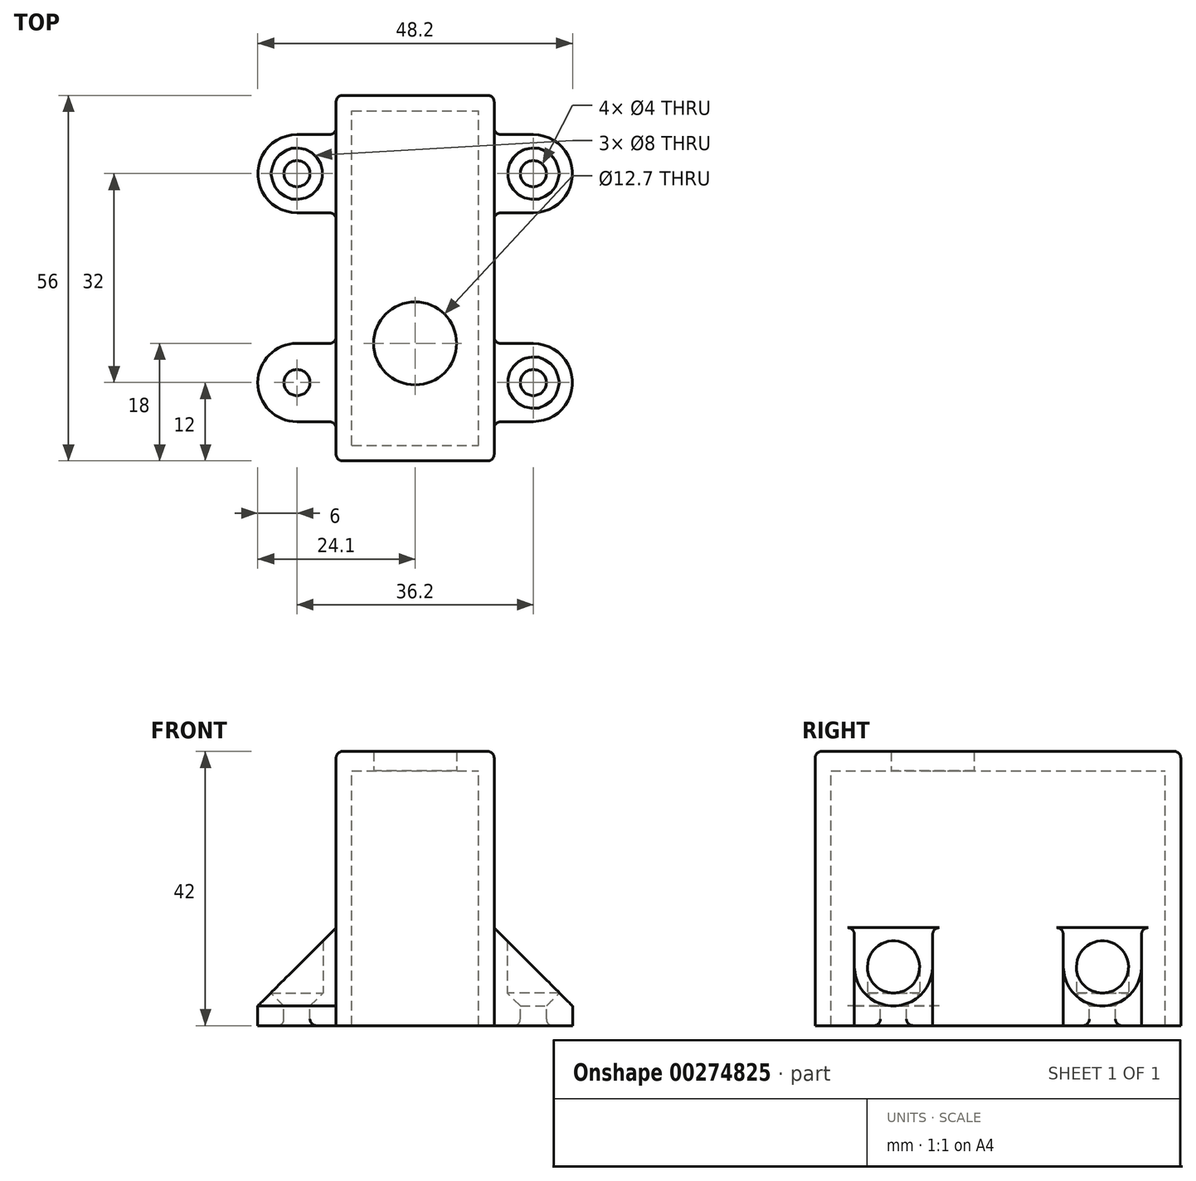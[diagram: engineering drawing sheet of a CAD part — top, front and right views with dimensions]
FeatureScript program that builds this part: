
annotation { "Feature Type Name" : "Feature", "Feature Type Description" : "" }
export const myFeature = defineFeature(function(context is Context, id is Id, definition is map)
    precondition{}
    {
        {
            var Q0;
            Q0=qCreatedBy(makeId("Top.planeOp"),FACE);
            var sketch = newSketch(context, id + "F0", { "sketchPlane" : qUnion([Q0])});
            skCircle(sketch, "E0", {"center": v(0, 0) * mm, "radius": 6.35 * mm});
            skLineSegment(sketch, "E1.bottom", {"start": v(8.1, 14) * mm, "end": v(-8.1, 14) * mm, "construction": true});
            skLineSegment(sketch, "E1.top", {"start": v(8.1, -14) * mm, "end": v(-8.1, -14) * mm, "construction": true});
            skLineSegment(sketch, "E1.left", {"start": v(8.1, 14) * mm, "end": v(8.1, -14) * mm, "construction": true});
            skLineSegment(sketch, "E1.right", {"start": v(-8.1, 14) * mm, "end": v(-8.1, -14) * mm, "construction": true});
            skCircle(sketch, "E2", {"center": v(0, 0) * mm, "radius": 5.9 * mm, "construction": true});
            skLineSegment(sketch, "E3.bottom", {"start": v(-7.1, 14) * mm, "end": v(-0.8, 14) * mm, "construction": true});
            skLineSegment(sketch, "E3.top", {"start": v(-7.1, 22.65) * mm, "end": v(-0.8, 22.65) * mm, "construction": true});
            skLineSegment(sketch, "E3.left", {"start": v(-7.1, 14) * mm, "end": v(-7.1, 22.65) * mm, "construction": true});
            skLineSegment(sketch, "E3.right", {"start": v(-0.8, 14) * mm, "end": v(-0.8, 22.65) * mm, "construction": true});
            skSolve(sketch);
        }
        {
            var Q0;
            Q0=qCreatedBy(makeId("Top.planeOp"),FACE);
            var sketch = newSketch(context, id + "F1", { "sketchPlane" : qUnion([Q0])});
            skLineSegment(sketch, "E4.bottom", {"start": v(12.1, 38) * mm, "end": v(-12.1, 38) * mm});
            skLineSegment(sketch, "E4.top", {"start": v(12.1, -18) * mm, "end": v(-12.1, -18) * mm});
            skLineSegment(sketch, "E4.left", {"start": v(12.1, 38) * mm, "end": v(12.1, -18) * mm});
            skLineSegment(sketch, "E4.right", {"start": v(-12.1, 38) * mm, "end": v(-12.1, -18) * mm});
            skPoint(sketch, "E4.middle", {"position": v(0, 10) * mm});
            skSolve(sketch);
        }
        {
            var Q0;
            Q0 = qSketchRegion(id + "F1", true);
            extrude(context, id + "F2", {"entities" : qUnion([Q0]), "depth" : 3 * mm});
        }
        {
            var Q0;
            Q0 = qSketchRegion(id + "F0", true);
            var Q1;
            Q1=makeQuery(id+"F2.opExtrude","CAP_FACE",FACE,{"disambiguationData":[OSD([sQuery(id+"F1.wireOp",EDGE,"E4.bottom"),sQuery(id+"F1.wireOp",EDGE,"E4.top"),sQuery(id+"F1.wireOp",EDGE,"E4.left"),sQuery(id+"F1.wireOp",EDGE,"E4.right")])],"isStart":false});
            extrude(context, id + "F3", {"entities" : qUnion([Q0]), "operationType" : NewBodyOperationType.REMOVE, "endBound" : BoundingType.UP_TO_SURFACE, "endBoundEntityFace" : qUnion([Q1]), "depth" : 25 * mm});
        }
        {
            var Q0;
            Q0=makeQuery(id+"F2.opExtrude","CAP_FACE",FACE,{"disambiguationData":[OSD([sQuery(id+"F1.wireOp",EDGE,"E4.bottom"),sQuery(id+"F1.wireOp",EDGE,"E4.top"),sQuery(id+"F1.wireOp",EDGE,"E4.left"),sQuery(id+"F1.wireOp",EDGE,"E4.right")])],"isStart":true});
            var sketch = newSketch(context, id + "F4", { "sketchPlane" : qUnion([Q0])});
            skLineSegment(sketch, "E5.bottom", {"start": v(-12.1, 18) * mm, "end": v(12.1, 18) * mm});
            skLineSegment(sketch, "E5.top", {"start": v(-12.1, -38) * mm, "end": v(12.1, -38) * mm});
            skLineSegment(sketch, "E5.left", {"start": v(-12.1, 18) * mm, "end": v(-12.1, -38) * mm});
            skLineSegment(sketch, "E5.right", {"start": v(12.1, 18) * mm, "end": v(12.1, -38) * mm});
            skLineSegment(sketch, "E6.bottom", {"start": v(-9.7, 15.6) * mm, "end": v(9.7, 15.6) * mm});
            skLineSegment(sketch, "E6.top", {"start": v(-9.7, -35.6) * mm, "end": v(9.7, -35.6) * mm});
            skLineSegment(sketch, "E6.left", {"start": v(-9.7, 15.6) * mm, "end": v(-9.7, -35.6) * mm});
            skLineSegment(sketch, "E6.right", {"start": v(9.7, 15.6) * mm, "end": v(9.7, -35.6) * mm});
            skSolve(sketch);
        }
        {
            var Q0;
            Q0 = qSketchRegion(id + "F4", true);
            extrude(context, id + "F5", {"entities" : qUnion([Q0]), "operationType" : NewBodyOperationType.ADD, "depth" : 36 * mm});
        }
        {
            var Q0;
            Q0=makeQuery(id+"F5.opExtrude","CAP_FACE",FACE,{"disambiguationData":[OSD([sQuery(id+"F4.wireOp",EDGE,"E5.bottom"),sQuery(id+"F4.wireOp",EDGE,"E5.top"),sQuery(id+"F4.wireOp",EDGE,"E5.left"),sQuery(id+"F4.wireOp",EDGE,"E5.right"),sQuery(id+"F4.wireOp",EDGE,"E6.bottom"),sQuery(id+"F4.wireOp",EDGE,"E6.top"),sQuery(id+"F4.wireOp",EDGE,"E6.left"),sQuery(id+"F4.wireOp",EDGE,"E6.right")])],"isStart":false});
            var sketch = newSketch(context, id + "F6", { "sketchPlane" : qUnion([Q0])});
            skLineSegment(sketch, "E7.bottom", {"start": v(-9.7, 15.6) * mm, "end": v(9.7, 15.6) * mm});
            skLineSegment(sketch, "E7.top", {"start": v(-9.7, -35.6) * mm, "end": v(9.7, -35.6) * mm});
            skLineSegment(sketch, "E7.left", {"start": v(-9.7, 15.6) * mm, "end": v(-9.7, -35.6) * mm});
            skLineSegment(sketch, "E7.right", {"start": v(9.7, 15.6) * mm, "end": v(9.7, -35.6) * mm});
            skLineSegment(sketch, "E8.bottom", {"start": v(-12.1, 18) * mm, "end": v(12.1, 18) * mm});
            skLineSegment(sketch, "E8.top", {"start": v(-12.1, -38) * mm, "end": v(12.1, -38) * mm});
            skLineSegment(sketch, "E8.left", {"start": v(-12.1, 18) * mm, "end": v(-12.1, 12) * mm});
            skLineSegment(sketch, "E8.right", {"start": v(12.1, 18) * mm, "end": v(12.1, -38) * mm});
            skArc(sketch, "E9", {"start": v(-18.1, 12) * mm, "mid": v(-24.1, 6) * mm, "end": v(-18.1, 0) * mm});
            skPoint(sketch, "E9.centerSnap0", {"position": v(-12.1, 6) * mm});
            skLineSegment(sketch, "E10.bottom", {"start": v(-18.1, 12) * mm, "end": v(-12.1, 12) * mm});
            skLineSegment(sketch, "E10.top", {"start": v(-18.1, 0) * mm, "end": v(-12.1, 0) * mm});
            skCircle(sketch, "E11", {"center": v(-18.1, 6) * mm, "radius": 2 * mm});
            skPoint(sketch, "E12.orphan", {"position": v(-6.1, 12) * mm});
            skPoint(sketch, "E13.orphan", {"position": v(-6.1, 0) * mm});
            skLineSegment(sketch, "E14.trimOffspring", {"start": v(-12.1, 0) * mm, "end": v(-12.1, -38) * mm});
            skLineSegment(sketch, "E15.MirrorCS", {"start": v(18.1, 12) * mm, "end": v(12.1, 12) * mm});
            skArc(sketch, "E16.MirrorCS", {"start": v(18.1, 12) * mm, "mid": v(24.1, 6) * mm, "end": v(18.1, 0) * mm});
            skLineSegment(sketch, "E17.MirrorCS", {"start": v(18.1, 0) * mm, "end": v(12.1, 0) * mm});
            skCircle(sketch, "E18.MirrorC", {"center": v(18.1, 6) * mm, "radius": 2 * mm});
            skLineSegment(sketch, "E19", {"start": v(38.2, 6) * mm, "end": v(-42.21, 6) * mm, "construction": true});
            skLineSegment(sketch, "E20", {"start": v(37.28, -10) * mm, "end": v(-33.25, -10) * mm, "construction": true});
            skPoint(sketch, "E20.startSnap0", {"position": v(12.1, -10) * mm});
            skLineSegment(sketch, "E21.MirrorCS", {"start": v(18.1, -20) * mm, "end": v(12.1, -20) * mm});
            skArc(sketch, "E22.MirrorCS", {"start": v(18.1, -32) * mm, "mid": v(24.1, -26) * mm, "end": v(18.1, -20) * mm});
            skLineSegment(sketch, "E23.MirrorCS", {"start": v(18.1, -32) * mm, "end": v(12.1, -32) * mm});
            skCircle(sketch, "E24.MirrorC", {"center": v(18.1, -26) * mm, "radius": 2 * mm});
            skLineSegment(sketch, "E25.MirrorCS", {"start": v(38.2, -26) * mm, "end": v(-42.21, -26) * mm, "construction": true});
            skLineSegment(sketch, "E26.MirrorCS", {"start": v(-18.1, -32) * mm, "end": v(-12.1, -32) * mm});
            skArc(sketch, "E27.MirrorCS", {"start": v(-18.1, -32) * mm, "mid": v(-24.1, -26) * mm, "end": v(-18.1, -20) * mm});
            skLineSegment(sketch, "E28.MirrorCS", {"start": v(-18.1, -20) * mm, "end": v(-12.1, -20) * mm});
            skCircle(sketch, "E29.MirrorC", {"center": v(-18.1, -26) * mm, "radius": 2 * mm});
            skSolve(sketch);
        }
        {
            var Q0;
            Q0 = qSketchRegion(id + "F6", true);
            extrude(context, id + "F7", {"entities" : qUnion([Q0]), "operationType" : NewBodyOperationType.ADD, "depth" : 3 * mm});
        }
        {
            var Q0;
            {var subQ2=sQuery(id+"F6.wireOp",EDGE,"E26.MirrorCS");var subQ6=sQuery(id+"F4.wireOp",EDGE,"E5.left");var subQ7=makeQuery(id+"F5.opExtrude","CAP_EDGE",EDGE,{"disambiguationData":[OSD([subQ6])],"isStart":false});Q0=makeQuery(id+"F7.boolean.opBoolean","SPLIT",EDGE,{"disambiguationData":[TD([makeQuery(id+"F7.opExtrude","SWEPT_FACE",FACE,{"disambiguationData":[OSD([subQ2])]})])],"derivedFrom":subQ7});}
            var Q1;
            {var subQ5=sQuery(id+"F6.wireOp",EDGE,"E10.bottom");var subQ7=sQuery(id+"F4.wireOp",EDGE,"E5.left");var subQ8=makeQuery(id+"F5.opExtrude","CAP_EDGE",EDGE,{"disambiguationData":[OSD([subQ7])],"isStart":false});Q1=makeQuery(id+"F7.boolean.opBoolean","SPLIT",EDGE,{"disambiguationData":[TD([makeQuery(id+"F7.opExtrude","SWEPT_FACE",FACE,{"disambiguationData":[OSD([subQ5])]})])],"derivedFrom":subQ8});}
            var Q2;
            {var subQ5=sQuery(id+"F6.wireOp",EDGE,"E15.MirrorCS");var subQ7=sQuery(id+"F4.wireOp",EDGE,"E5.right");Q2=makeQuery(id+"F7.boolean.opBoolean","SPLIT",EDGE,{"disambiguationData":[TD([makeQuery(id+"F7.opExtrude","SWEPT_FACE",FACE,{"disambiguationData":[OSD([subQ5])]})])],"derivedFrom":makeQuery(id+"F5.opExtrude","CAP_EDGE",EDGE,{"disambiguationData":[OSD([subQ7])],"isStart":false})});}
            var Q3;
            {var subQ3=sQuery(id+"F6.wireOp",EDGE,"E21.MirrorCS");var subQ7=sQuery(id+"F4.wireOp",EDGE,"E5.right");Q3=makeQuery(id+"F7.boolean.opBoolean","SPLIT",EDGE,{"disambiguationData":[TD([makeQuery(id+"F7.opExtrude","SWEPT_FACE",FACE,{"disambiguationData":[OSD([subQ3])]})])],"derivedFrom":makeQuery(id+"F5.opExtrude","CAP_EDGE",EDGE,{"disambiguationData":[OSD([subQ7])],"isStart":false})});}
            chamfer(context, id + "F8", {"entities" : qUnion([Q0, Q1, Q2, Q3]), "width" : 12 * mm, "tangentPropagation" : true});
        }
        {
            var Q0;
            Q0=makeQuery(id+"F7.opExtrude","CAP_FACE",FACE,{"disambiguationData":[OSD([sQuery(id+"F6.wireOp",EDGE,"E7.bottom"),sQuery(id+"F6.wireOp",EDGE,"E7.top"),sQuery(id+"F6.wireOp",EDGE,"E7.left"),sQuery(id+"F6.wireOp",EDGE,"E7.right"),sQuery(id+"F6.wireOp",EDGE,"E8.bottom"),sQuery(id+"F6.wireOp",EDGE,"E8.top"),sQuery(id+"F6.wireOp",EDGE,"E8.left"),sQuery(id+"F6.wireOp",EDGE,"E8.right"),sQuery(id+"F6.wireOp",EDGE,"E9"),sQuery(id+"F6.wireOp",EDGE,"E10.bottom"),sQuery(id+"F6.wireOp",EDGE,"E10.top"),sQuery(id+"F6.wireOp",EDGE,"E11"),sQuery(id+"F6.wireOp",EDGE,"E14.trimOffspring"),sQuery(id+"F6.wireOp",EDGE,"E15.MirrorCS"),sQuery(id+"F6.wireOp",EDGE,"E16.MirrorCS"),sQuery(id+"F6.wireOp",EDGE,"E17.MirrorCS"),sQuery(id+"F6.wireOp",EDGE,"E18.MirrorC"),sQuery(id+"F6.wireOp",EDGE,"E21.MirrorCS"),sQuery(id+"F6.wireOp",EDGE,"E22.MirrorCS"),sQuery(id+"F6.wireOp",EDGE,"E23.MirrorCS"),sQuery(id+"F6.wireOp",EDGE,"E24.MirrorC"),sQuery(id+"F6.wireOp",EDGE,"E26.MirrorCS"),sQuery(id+"F6.wireOp",EDGE,"E27.MirrorCS"),sQuery(id+"F6.wireOp",EDGE,"E28.MirrorCS"),sQuery(id+"F6.wireOp",EDGE,"E29.MirrorC")])],"isStart":false});
            cPlane(context, id + "F9", {"entities" : qUnion([Q0]), "cplaneType" : CPlaneType.OFFSET, "offset" : 3 * mm, "oppositeDirection" : true, "width" : 150 * mm, "height" : 150 * mm});
        }
        {
            var Q0;
            Q0=qCreatedBy(id+"F9.planeOp",FACE);
            var sketch = newSketch(context, id + "F10", { "sketchPlane" : qUnion([Q0])});
            skLineSegment(sketch, "E30", {"start": v(18.1, -42.57) * mm, "end": v(18.1, 21.83) * mm, "construction": true});
            skLineSegment(sketch, "E31", {"start": v(-18.1, -40.05) * mm, "end": v(-18.1, 19.87) * mm, "construction": true});
            skLineSegment(sketch, "E32", {"start": v(28.5, -26) * mm, "end": v(-28.53, -26) * mm, "construction": true});
            skLineSegment(sketch, "E33", {"start": v(28.5, 6) * mm, "end": v(-28.53, 6) * mm, "construction": true});
            skCircle(sketch, "E34", {"center": v(18.1, -26) * mm, "radius": 4 * mm});
            skCircle(sketch, "E35", {"center": v(18.1, 6) * mm, "radius": 4 * mm});
            skCircle(sketch, "E36", {"center": v(-18.1, -26) * mm, "radius": 4 * mm});
            skCircle(sketch, "E37", {"center": v(-18.1, 6) * mm, "radius": 4 * mm});
            skSolve(sketch);
        }
        {
            var Q0;
            Q0 = qSketchRegion(id + "F10", true);
            var Q1;
            {var subQ2=sQuery(id+"F6.wireOp",EDGE,"E26.MirrorCS");var subQ6=sQuery(id+"F4.wireOp",EDGE,"E5.left");var subQ7=makeQuery(id+"F5.opExtrude","CAP_EDGE",EDGE,{"disambiguationData":[OSD([subQ6])],"isStart":false});Q1=makeQuery(id+"F8.opChamfer","BLEND_FACE",FACE,{"disambiguationData":[OSD([subQ6]),TDD([makeQuery(id+"F7.boolean.opBoolean","SPLIT",EDGE,{"disambiguationData":[TD([makeQuery(id+"F7.opExtrude","SWEPT_FACE",FACE,{"disambiguationData":[OSD([subQ2])]})])],"derivedFrom":subQ7})])]});}
            extrude(context, id + "F11", {"entities" : qUnion([Q0]), "operationType" : NewBodyOperationType.REMOVE, "endBound" : BoundingType.UP_TO_SURFACE, "oppositeDirection" : true, "endBoundEntityFace" : qUnion([Q1]), "depth" : 25 * mm});
        }
        {
            var Q0;
            Q0=makeQuery(id+"F11.boolean.opBoolean","COPY",EDGE,{"derivedFrom":makeQuery(id+"F11.opExtrude","CAP_EDGE",EDGE,{"disambiguationData":[OSD([sQuery(id+"F10.wireOp",EDGE,"E35")])],"isStart":true})});
            var Q1;
            Q1=makeQuery(id+"F11.boolean.opBoolean","COPY",EDGE,{"derivedFrom":makeQuery(id+"F11.opExtrude","CAP_EDGE",EDGE,{"disambiguationData":[OSD([sQuery(id+"F10.wireOp",EDGE,"E34")])],"isStart":true})});
            var Q2;
            Q2=makeQuery(id+"F11.boolean.opBoolean","COPY",EDGE,{"derivedFrom":makeQuery(id+"F11.opExtrude","CAP_EDGE",EDGE,{"disambiguationData":[OSD([sQuery(id+"F10.wireOp",EDGE,"E37")])],"isStart":true})});
            var Q3;
            Q3=makeQuery(id+"F11.boolean.opBoolean","COPY",EDGE,{"derivedFrom":makeQuery(id+"F11.opExtrude","CAP_EDGE",EDGE,{"disambiguationData":[OSD([sQuery(id+"F10.wireOp",EDGE,"E36")])],"isStart":true})});
            chamfer(context, id + "F12", {"entities" : qUnion([Q0, Q1, Q2, Q3]), "width" : 2 * mm, "tangentPropagation" : true});
        }
        {
            var Q0;
            Q0=makeQuery(id+"F7.boolean.opBoolean","MERGE",EDGE,{"derivedFrom":[makeQuery(id+"F5.boolean.opBoolean","MERGE",EDGE,{"derivedFrom":[makeQuery(id+"F2.opExtrude","SWEPT_EDGE",EDGE,{"disambiguationData":[OSD([sQuery(id+"F1.wireOp",EDGE,"E4.bottom"),sQuery(id+"F1.wireOp",EDGE,"E4.right")])]}),makeQuery(id+"F5.opExtrude","SWEPT_EDGE",EDGE,{"disambiguationData":[OSD([sQuery(id+"F4.wireOp",EDGE,"E5.top"),sQuery(id+"F4.wireOp",EDGE,"E5.left")])]})]}),makeQuery(id+"F7.opExtrude","SWEPT_EDGE",EDGE,{"disambiguationData":[OSD([sQuery(id+"F6.wireOp",EDGE,"E8.top"),sQuery(id+"F6.wireOp",EDGE,"E14.trimOffspring")])]})]});
            var Q1;
            Q1=makeQuery(id+"F7.boolean.opBoolean","MERGE",EDGE,{"derivedFrom":[makeQuery(id+"F5.boolean.opBoolean","MERGE",EDGE,{"derivedFrom":[makeQuery(id+"F2.opExtrude","SWEPT_EDGE",EDGE,{"disambiguationData":[OSD([sQuery(id+"F1.wireOp",EDGE,"E4.bottom"),sQuery(id+"F1.wireOp",EDGE,"E4.left")])]}),makeQuery(id+"F5.opExtrude","SWEPT_EDGE",EDGE,{"disambiguationData":[OSD([sQuery(id+"F4.wireOp",EDGE,"E5.top"),sQuery(id+"F4.wireOp",EDGE,"E5.right")])]})]}),makeQuery(id+"F7.opExtrude","SWEPT_EDGE",EDGE,{"disambiguationData":[OSD([sQuery(id+"F6.wireOp",EDGE,"E8.top"),sQuery(id+"F6.wireOp",EDGE,"E8.right")])]})]});
            var Q2;
            Q2=makeQuery(id+"F2.opExtrude","CAP_EDGE",EDGE,{"disambiguationData":[OSD([sQuery(id+"F1.wireOp",EDGE,"E4.bottom")])],"isStart":false});
            var Q3;
            Q3=makeQuery(id+"F2.opExtrude","CAP_EDGE",EDGE,{"disambiguationData":[OSD([sQuery(id+"F1.wireOp",EDGE,"E4.right")])],"isStart":false});
            var Q4;
            Q4=makeQuery(id+"F2.opExtrude","CAP_EDGE",EDGE,{"disambiguationData":[OSD([sQuery(id+"F1.wireOp",EDGE,"E4.left")])],"isStart":false});
            var Q5;
            Q5=makeQuery(id+"F2.opExtrude","CAP_EDGE",EDGE,{"disambiguationData":[OSD([sQuery(id+"F1.wireOp",EDGE,"E4.top")])],"isStart":false});
            var Q6;
            Q6=makeQuery(id+"F7.boolean.opBoolean","MERGE",EDGE,{"derivedFrom":[makeQuery(id+"F5.boolean.opBoolean","MERGE",EDGE,{"derivedFrom":[makeQuery(id+"F2.opExtrude","SWEPT_EDGE",EDGE,{"disambiguationData":[OSD([sQuery(id+"F1.wireOp",EDGE,"E4.top"),sQuery(id+"F1.wireOp",EDGE,"E4.left")])]}),makeQuery(id+"F5.opExtrude","SWEPT_EDGE",EDGE,{"disambiguationData":[OSD([sQuery(id+"F4.wireOp",EDGE,"E5.bottom"),sQuery(id+"F4.wireOp",EDGE,"E5.right")])]})]}),makeQuery(id+"F7.opExtrude","SWEPT_EDGE",EDGE,{"disambiguationData":[OSD([sQuery(id+"F6.wireOp",EDGE,"E8.bottom"),sQuery(id+"F6.wireOp",EDGE,"E8.right")])]})]});
            var Q7;
            Q7=makeQuery(id+"F7.boolean.opBoolean","MERGE",EDGE,{"derivedFrom":[makeQuery(id+"F5.boolean.opBoolean","MERGE",EDGE,{"derivedFrom":[makeQuery(id+"F2.opExtrude","SWEPT_EDGE",EDGE,{"disambiguationData":[OSD([sQuery(id+"F1.wireOp",EDGE,"E4.top"),sQuery(id+"F1.wireOp",EDGE,"E4.right")])]}),makeQuery(id+"F5.opExtrude","SWEPT_EDGE",EDGE,{"disambiguationData":[OSD([sQuery(id+"F4.wireOp",EDGE,"E5.bottom"),sQuery(id+"F4.wireOp",EDGE,"E5.left")])]})]}),makeQuery(id+"F7.opExtrude","SWEPT_EDGE",EDGE,{"disambiguationData":[OSD([sQuery(id+"F6.wireOp",EDGE,"E8.bottom"),sQuery(id+"F6.wireOp",EDGE,"E8.left")])]})]});
            var Q8;
            Q8=makeQuery(id+"F7.opExtrude","SWEPT_EDGE",EDGE,{"disambiguationData":[OSD([sQuery(id+"F6.wireOp",EDGE,"E14.trimOffspring"),sQuery(id+"F6.wireOp",EDGE,"E26.MirrorCS")])]});
            var Q9;
            Q9=makeQuery(id+"F7.opExtrude","SWEPT_EDGE",EDGE,{"disambiguationData":[OSD([sQuery(id+"F4.wireOp",EDGE,"E5.left"),sQuery(id+"F6.wireOp",EDGE,"E10.top"),sQuery(id+"F6.wireOp",EDGE,"E14.trimOffspring")])]});
            var Q10;
            Q10=makeQuery(id+"F7.opExtrude","SWEPT_EDGE",EDGE,{"disambiguationData":[OSD([sQuery(id+"F6.wireOp",EDGE,"E14.trimOffspring"),sQuery(id+"F6.wireOp",EDGE,"E28.MirrorCS")])]});
            var Q11;
            Q11=makeQuery(id+"F7.opExtrude","SWEPT_EDGE",EDGE,{"disambiguationData":[OSD([sQuery(id+"F4.wireOp",EDGE,"E5.left"),sQuery(id+"F6.wireOp",EDGE,"E8.left"),sQuery(id+"F6.wireOp",EDGE,"E10.bottom")])]});
            var Q12;
            Q12=makeQuery(id+"F7.opExtrude","SWEPT_EDGE",EDGE,{"disambiguationData":[OSD([sQuery(id+"F6.wireOp",EDGE,"E8.right"),sQuery(id+"F6.wireOp",EDGE,"E15.MirrorCS")])]});
            var Q13;
            Q13=makeQuery(id+"F7.opExtrude","SWEPT_EDGE",EDGE,{"disambiguationData":[OSD([sQuery(id+"F6.wireOp",EDGE,"E8.right"),sQuery(id+"F6.wireOp",EDGE,"E21.MirrorCS")])]});
            var Q14;
            Q14=makeQuery(id+"F7.opExtrude","SWEPT_EDGE",EDGE,{"disambiguationData":[OSD([sQuery(id+"F6.wireOp",EDGE,"E8.right"),sQuery(id+"F6.wireOp",EDGE,"E17.MirrorCS")])]});
            var Q15;
            Q15=makeQuery(id+"F7.opExtrude","SWEPT_EDGE",EDGE,{"disambiguationData":[OSD([sQuery(id+"F6.wireOp",EDGE,"E8.right"),sQuery(id+"F6.wireOp",EDGE,"E23.MirrorCS")])]});
            var Q16;
            Q16=makeQuery(id+"F7.opExtrude","CAP_EDGE",EDGE,{"disambiguationData":[OSD([sQuery(id+"F6.wireOp",EDGE,"E18.MirrorC")])],"isStart":false});
            var Q17;
            Q17=makeQuery(id+"F7.opExtrude","CAP_EDGE",EDGE,{"disambiguationData":[OSD([sQuery(id+"F6.wireOp",EDGE,"E24.MirrorC")])],"isStart":false});
            var Q18;
            Q18=makeQuery(id+"F7.opExtrude","CAP_EDGE",EDGE,{"disambiguationData":[OSD([sQuery(id+"F6.wireOp",EDGE,"E29.MirrorC")])],"isStart":false});
            var Q19;
            Q19=makeQuery(id+"F7.opExtrude","CAP_EDGE",EDGE,{"disambiguationData":[OSD([sQuery(id+"F6.wireOp",EDGE,"E11")])],"isStart":false});
            fillet(context, id + "F13", {"entities" : qUnion([Q0, Q1, Q2, Q3, Q4, Q5, Q6, Q7, Q8, Q9, Q10, Q11, Q12, Q13, Q14, Q15, Q16, Q17, Q18, Q19]), "radius" : 1 * mm, "tangentPropagation" : true, "allowEdgeOverflow" : false});
        }
    });
